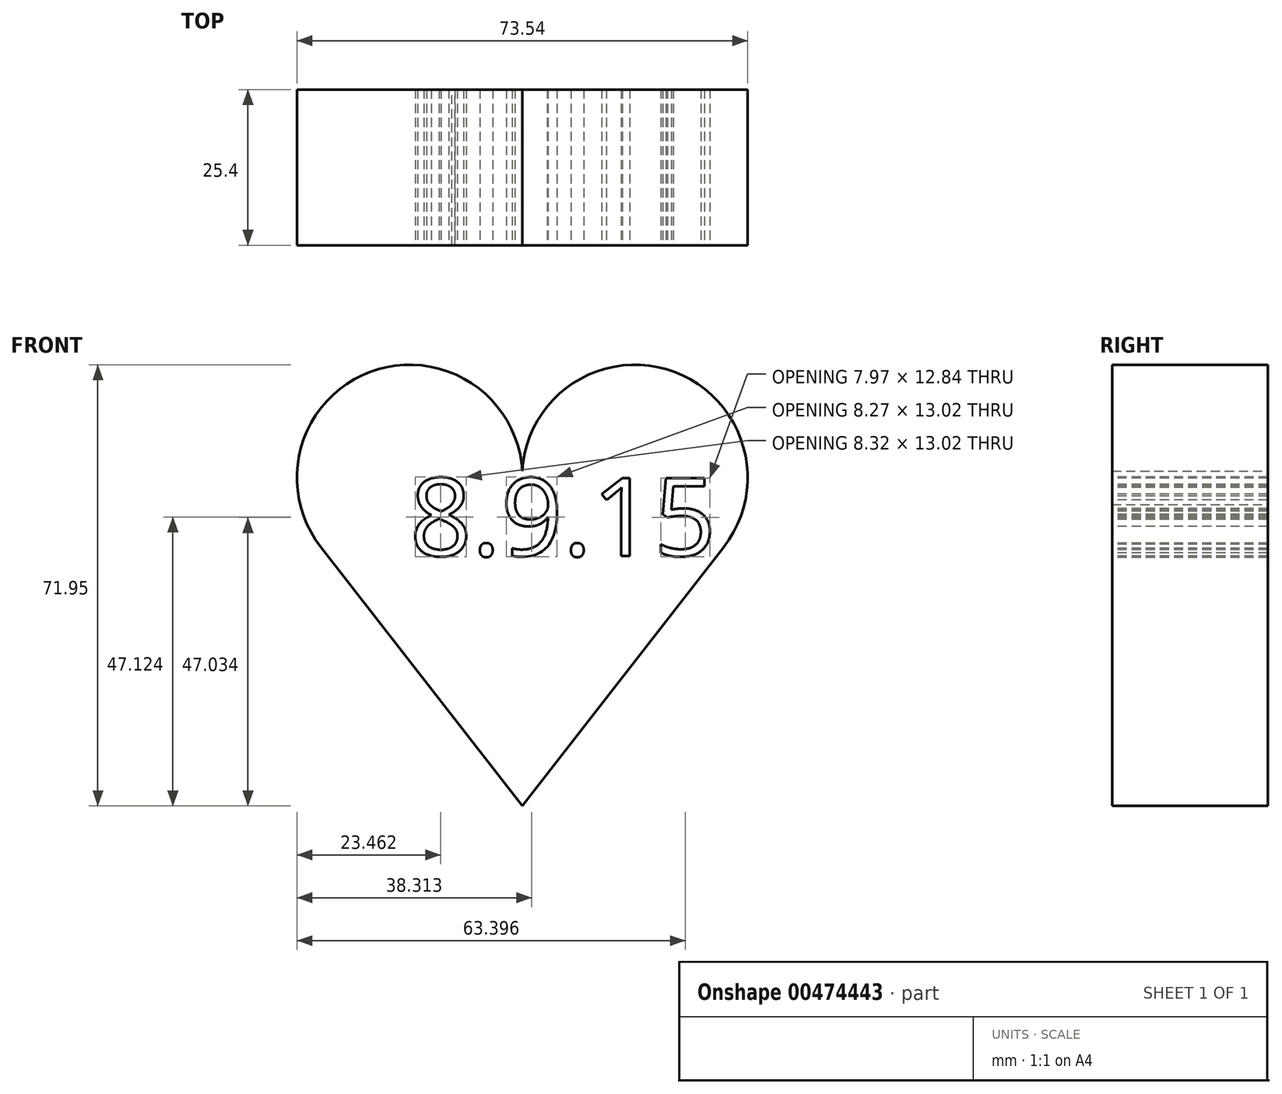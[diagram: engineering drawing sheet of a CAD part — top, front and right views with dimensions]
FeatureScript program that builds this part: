
annotation { "Feature Type Name" : "Feature", "Feature Type Description" : "" }
export const myFeature = defineFeature(function(context is Context, id is Id, definition is map)
    precondition{}
    {
        {
            var Q0;
            Q0=qCreatedBy(makeId("Front.planeOp"),FACE);
            var sketch = newSketch(context, id + "F0", { "sketchPlane" : qUnion([Q0])});
            skArc(sketch, "E0", {"start": v(32.89, 6.9) * mm, "mid": v(24.85, 35.41) * mm, "end": v(0, 19.27) * mm});
            skLineSegment(sketch, "E1", {"start": v(0, 19.27) * mm, "end": v(0, -35.36) * mm});
            skLineSegment(sketch, "E2", {"start": v(0, -35.36) * mm, "end": v(32.89, 6.9) * mm});
            skArc(sketch, "E3.MirrorCS", {"start": v(-32.89, 6.9) * mm, "mid": v(-24.85, 35.41) * mm, "end": v(0, 19.27) * mm});
            skLineSegment(sketch, "E4.MirrorCS", {"start": v(0, -35.36) * mm, "end": v(-32.89, 6.9) * mm});
            skSolve(sketch);
        }
        {
            var Q0;
            Q0=makeQuery(id+"F0.imprint","IMPRINT",FACE,{"disambiguationData":[TD([[makeQuery(id+"F0.imprint","IMPRINT",EDGE,{"derivedFrom":sQuery(id+"F0.wireOp",EDGE,"E1")}),-1.0]])]});
            var Q1;
            Q1=makeQuery(id+"F0.imprint","IMPRINT",FACE,{"disambiguationData":[TD([[makeQuery(id+"F0.imprint","IMPRINT",EDGE,{"derivedFrom":sQuery(id+"F0.wireOp",EDGE,"E0")}),1.0]])]});
            extrude(context, id + "F1", {"entities" : qUnion([Q0, Q1]), "depth" : 25.4 * mm});
        }
        {
            var Q0;
            Q0=makeQuery(id+"F1.opExtrude","CAP_FACE",FACE,{"disambiguationData":[OSD([sQuery(id+"F0.wireOp",EDGE,"E0"),sQuery(id+"F0.wireOp",EDGE,"E2"),sQuery(id+"F0.wireOp",EDGE,"E3.MirrorCS"),sQuery(id+"F0.wireOp",EDGE,"E4.MirrorCS")])],"isStart":false});
            var sketch = newSketch(context, id + "F2", { "sketchPlane" : qUnion([Q0])});
            skText(sketch, "E5", { "text": "8.9.15", "fontName": "OpenSans-Regular.ttf"});
            const initialGuessF2  = {"E5": [-0.01837, 0.00543, 1, 0, 0.01277]};
            skSetInitialGuess(sketch, initialGuessF2);
            skSolve(sketch);
        }
        {
            var Q0;
            Q0 = qSketchRegion(id + "F2", true);
            extrude(context, id + "F3", {"entities" : qUnion([Q0]), "operationType" : NewBodyOperationType.REMOVE, "oppositeDirection" : true, "depth" : 25.4 * mm});
        }
    });
